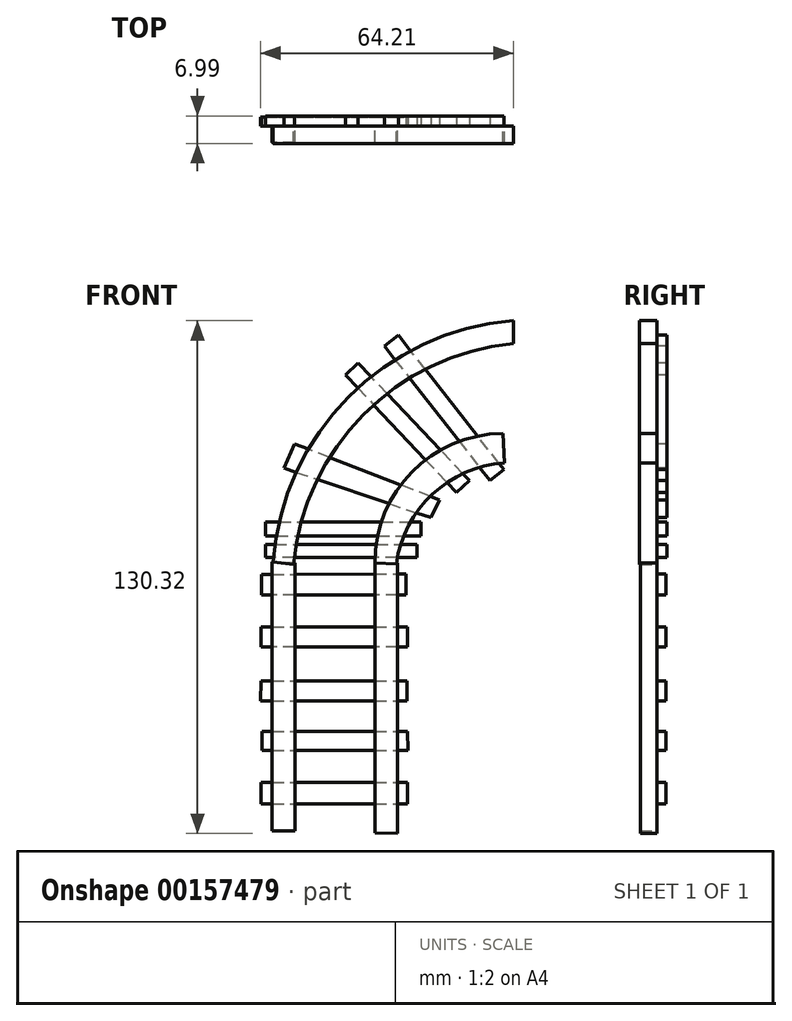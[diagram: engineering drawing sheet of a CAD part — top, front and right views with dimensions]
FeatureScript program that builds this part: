
annotation { "Feature Type Name" : "Feature", "Feature Type Description" : "" }
export const myFeature = defineFeature(function(context is Context, id is Id, definition is map)
    precondition{}
    {
        {
            var Q0;
            Q0=qCreatedBy(makeId("Front.planeOp"),FACE);
            var sketch = newSketch(context, id + "F0", { "sketchPlane" : qUnion([Q0])});
            skLineSegment(sketch, "E0", {"start": v(-63.76, 56) * mm, "end": v(-63.76, -12.32) * mm});
            skLineSegment(sketch, "E1", {"start": v(-63.76, -12.32) * mm, "end": v(-57.96, -12.32) * mm});
            skLineSegment(sketch, "E2", {"start": v(-57.96, -12.32) * mm, "end": v(-57.96, 55.79) * mm});
            skLineSegment(sketch, "E3", {"start": v(-57.96, 55.79) * mm, "end": v(-63.76, 56) * mm});
            skLineSegment(sketch, "E4", {"start": v(-37.68, -12.73) * mm, "end": v(-37.68, 55.79) * mm});
            skLineSegment(sketch, "E5", {"start": v(-37.68, 55.79) * mm, "end": v(-31.88, 55.79) * mm});
            skLineSegment(sketch, "E6", {"start": v(-31.88, 55.79) * mm, "end": v(-31.88, -12.94) * mm});
            skLineSegment(sketch, "E7", {"start": v(-37.68, -12.73) * mm, "end": v(-31.88, -12.94) * mm});
            skSolve(sketch);
        }
        {
            var Q0;
            Q0 = qSketchRegion(id + "F0", true);
            extrude(context, id + "F1", {"entities" : qUnion([Q0]), "depth" : 4.2 * mm});
        }
        {
            var Q0;
            Q0=qCreatedBy(makeId("Front.planeOp"),FACE);
            var sketch = newSketch(context, id + "F2", { "sketchPlane" : qUnion([Q0])});
            skLineSegment(sketch, "E8", {"start": v(-66.56, 0) * mm, "end": v(-29.34, 0) * mm});
            skLineSegment(sketch, "E9", {"start": v(-66.56, -5.44) * mm, "end": v(-66.56, 0) * mm});
            skLineSegment(sketch, "E10", {"start": v(-66.56, -5.44) * mm, "end": v(-29.33, -5.44) * mm});
            skLineSegment(sketch, "E11", {"start": v(-29.34, 0) * mm, "end": v(-29.33, -5.44) * mm});
            skLineSegment(sketch, "E12", {"start": v(-66.35, 13.03) * mm, "end": v(-29.4, 13.03) * mm});
            skLineSegment(sketch, "E13", {"start": v(-66.65, 25.86) * mm, "end": v(-29.5, 25.86) * mm});
            skLineSegment(sketch, "E14", {"start": v(-66.7, 20.8) * mm, "end": v(-29.44, 20.8) * mm});
            skLineSegment(sketch, "E15", {"start": v(-29.44, 20.8) * mm, "end": v(-29.5, 25.86) * mm});
            skLineSegment(sketch, "E16", {"start": v(-66.7, 20.8) * mm, "end": v(-66.65, 25.86) * mm});
            skLineSegment(sketch, "E17", {"start": v(-66.65, 39.59) * mm, "end": v(-29.32, 39.59) * mm});
            skLineSegment(sketch, "E18", {"start": v(-29.32, 39.59) * mm, "end": v(-29.32, 34.42) * mm});
            skLineSegment(sketch, "E19", {"start": v(-29.32, 34.42) * mm, "end": v(-66.64, 34.42) * mm});
            skLineSegment(sketch, "E20", {"start": v(-66.64, 34.42) * mm, "end": v(-66.65, 39.59) * mm});
            skLineSegment(sketch, "E21", {"start": v(-66.48, 52.94) * mm, "end": v(-29.72, 52.97) * mm});
            skLineSegment(sketch, "E22", {"start": v(-29.72, 52.97) * mm, "end": v(-29.72, 47.65) * mm});
            skLineSegment(sketch, "E23", {"start": v(-29.72, 47.65) * mm, "end": v(-66.48, 47.65) * mm});
            skLineSegment(sketch, "E24", {"start": v(-66.48, 47.65) * mm, "end": v(-66.48, 52.94) * mm});
            skLineSegment(sketch, "E25", {"start": v(-66.35, 13.03) * mm, "end": v(-66.35, 8.18) * mm});
            skLineSegment(sketch, "E26", {"start": v(-66.35, 8.18) * mm, "end": v(-29.25, 8.18) * mm});
            skLineSegment(sketch, "E27", {"start": v(-29.4, 13.03) * mm, "end": v(-29.25, 8.18) * mm});
            skSolve(sketch);
        }
        {
            var Q0;
            Q0 = qSketchRegion(id + "F2", true);
            extrude(context, id + "F3", {"entities" : qUnion([Q0]), "oppositeDirection" : true, "depth" : 2.3 * mm});
        }
        {
            var Q0;
            Q0=qCreatedBy(makeId("Front.planeOp"),FACE);
            var sketch = newSketch(context, id + "F4", { "sketchPlane" : qUnion([Q0])});
            skArc(sketch, "E28", {"start": v(-2.48, 117.38) * mm, "mid": v(-44.36, 97.97) * mm, "end": v(-63.55, 56) * mm});
            skArc(sketch, "E29", {"start": v(-2.48, 111.6) * mm, "mid": v(-40.53, 93.53) * mm, "end": v(-58.38, 55.38) * mm});
            skArc(sketch, "E30", {"start": v(-5.18, 88.7) * mm, "mid": v(-28.23, 78.96) * mm, "end": v(-37.68, 55.79) * mm});
            skArc(sketch, "E31", {"start": v(-4.77, 81.19) * mm, "mid": v(-23.04, 73.27) * mm, "end": v(-32.23, 55.6) * mm});
            skLineSegment(sketch, "E32", {"start": v(-2.48, 117.38) * mm, "end": v(-2.48, 111.6) * mm});
            skLineSegment(sketch, "E33", {"start": v(-5.18, 88.7) * mm, "end": v(-4.77, 81.19) * mm});
            skLineSegment(sketch, "E34", {"start": v(-63.55, 56) * mm, "end": v(-58.38, 55.38) * mm});
            skLineSegment(sketch, "E35", {"start": v(-37.68, 55.79) * mm, "end": v(-32.23, 55.6) * mm});
            skSolve(sketch);
        }
        {
            var Q0;
            Q0 = qSketchRegion(id + "F4", true);
            extrude(context, id + "F5", {"entities" : qUnion([Q0]), "depth" : 4.44 * mm});
        }
        {
            var Q0;
            Q0=qCreatedBy(makeId("Front.planeOp"),FACE);
            var sketch = newSketch(context, id + "F6", { "sketchPlane" : qUnion([Q0])});
            skLineSegment(sketch, "E36", {"start": v(-65.43, 60.48) * mm, "end": v(-65.43, 60.48) * mm});
            skLineSegment(sketch, "E37", {"start": v(-65.43, 60.48) * mm, "end": v(-26.91, 60.48) * mm});
            skLineSegment(sketch, "E38", {"start": v(-26.91, 60.48) * mm, "end": v(-26.91, 57.15) * mm});
            skLineSegment(sketch, "E39", {"start": v(-26.91, 57.15) * mm, "end": v(-65.38, 57.15) * mm});
            skLineSegment(sketch, "E40", {"start": v(-60.74, 79.9) * mm, "end": v(-23.4, 67.3) * mm});
            skLineSegment(sketch, "E41", {"start": v(-23.4, 67.3) * mm, "end": v(-21.3, 71.87) * mm});
            skLineSegment(sketch, "E42", {"start": v(-21.3, 71.87) * mm, "end": v(-58.06, 86.05) * mm});
            skLineSegment(sketch, "E43", {"start": v(-45.11, 103.56) * mm, "end": v(-16.89, 73.69) * mm});
            skLineSegment(sketch, "E44", {"start": v(-16.89, 73.69) * mm, "end": v(-13.67, 76.73) * mm});
            skLineSegment(sketch, "E45", {"start": v(-13.67, 76.73) * mm, "end": v(-41.93, 106.63) * mm});
            skLineSegment(sketch, "E46", {"start": v(-35.23, 110.9) * mm, "end": v(-8.41, 76.73) * mm});
            skLineSegment(sketch, "E47", {"start": v(-8.41, 76.73) * mm, "end": v(-4.86, 79.51) * mm});
            skLineSegment(sketch, "E48", {"start": v(-4.86, 79.51) * mm, "end": v(-31.68, 113.7) * mm});
            skLineSegment(sketch, "E49", {"start": v(-31.68, 113.7) * mm, "end": v(-35.23, 110.9) * mm});
            skLineSegment(sketch, "E50", {"start": v(-41.93, 106.63) * mm, "end": v(-45.11, 103.56) * mm});
            skLineSegment(sketch, "E51", {"start": v(-58.06, 86.05) * mm, "end": v(-60.74, 79.9) * mm});
            skLineSegment(sketch, "E52", {"start": v(-65.43, 60.48) * mm, "end": v(-65.38, 57.15) * mm});
            skLineSegment(sketch, "E53", {"start": v(-65.43, 66.21) * mm, "end": v(-65.43, 62.7) * mm});
            skLineSegment(sketch, "E54", {"start": v(-65.43, 62.7) * mm, "end": v(-26, 62.7) * mm});
            skLineSegment(sketch, "E55", {"start": v(-65.43, 66.21) * mm, "end": v(-26, 66.21) * mm});
            skLineSegment(sketch, "E56", {"start": v(-26, 66.21) * mm, "end": v(-26, 62.7) * mm});
            skSolve(sketch);
        }
        {
            var Q0;
            Q0 = qSketchRegion(id + "F6", true);
            extrude(context, id + "F7", {"entities" : qUnion([Q0]), "oppositeDirection" : true, "depth" : 2.54 * mm});
        }
    });
